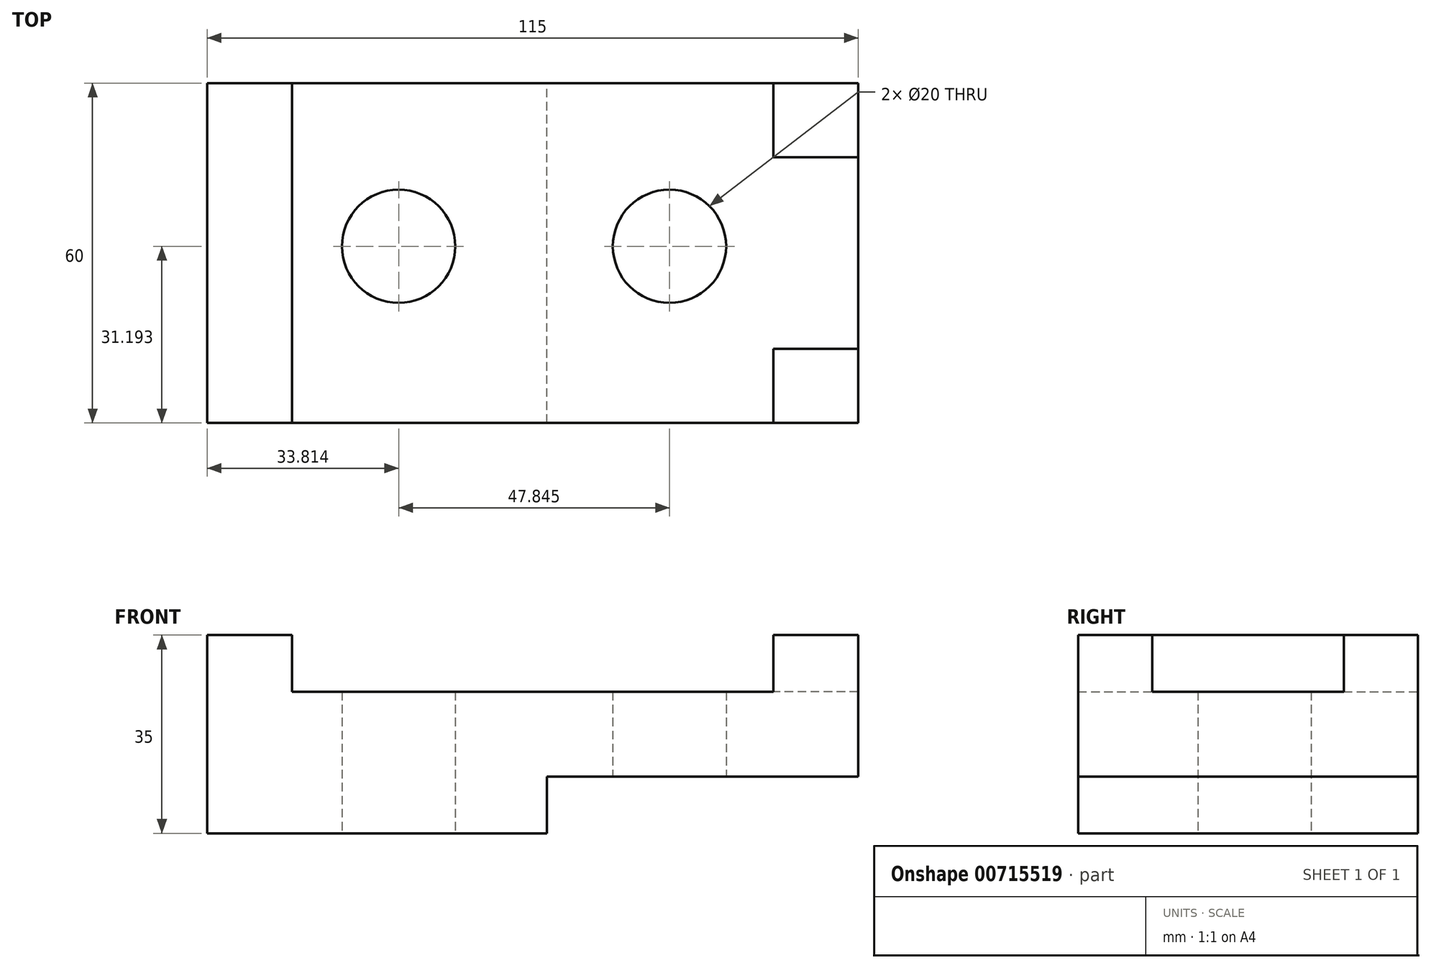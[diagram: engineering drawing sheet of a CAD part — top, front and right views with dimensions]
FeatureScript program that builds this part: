
annotation { "Feature Type Name" : "Feature", "Feature Type Description" : "" }
export const myFeature = defineFeature(function(context is Context, id is Id, definition is map)
    precondition{}
    {
        {
            var Q0;
            Q0=qCreatedBy(makeId("Front.planeOp"),FACE);
            var sketch = newSketch(context, id + "F0", { "sketchPlane" : qUnion([Q0])});
            skLineSegment(sketch, "E0", {"start": v(-60, 0) * mm, "end": v(0, 0) * mm});
            skLineSegment(sketch, "E1", {"start": v(0, 0) * mm, "end": v(0, 10) * mm});
            skLineSegment(sketch, "E2", {"start": v(0, 10) * mm, "end": v(55, 10) * mm});
            skLineSegment(sketch, "E3", {"start": v(-60, 0) * mm, "end": v(-60, 35) * mm});
            skLineSegment(sketch, "E4", {"start": v(-60, 35) * mm, "end": v(-45, 35) * mm});
            skLineSegment(sketch, "E5", {"start": v(-45, 35) * mm, "end": v(-45, 25) * mm});
            skLineSegment(sketch, "E6", {"start": v(-45, 25) * mm, "end": v(40, 25) * mm});
            skLineSegment(sketch, "E7", {"start": v(40, 25) * mm, "end": v(40, 35) * mm});
            skLineSegment(sketch, "E8", {"start": v(40, 35) * mm, "end": v(55, 35) * mm});
            skLineSegment(sketch, "E9", {"start": v(55, 35) * mm, "end": v(55, 10) * mm});
            skSolve(sketch);
        }
        {
            var Q0;
            Q0=makeQuery(id+"F0.imprint","IMPRINT",FACE,{"disambiguationData":[TD([[makeQuery(id+"F0.imprint","IMPRINT",EDGE,{"derivedFrom":sQuery(id+"F0.wireOp",EDGE,"E0")}),1.0]])]});
            extrude(context, id + "F1", {"entities" : qUnion([Q0]), "depth" : 60 * mm, "offsetDistance" : 25 * mm});
        }
        {
            var Q0;
            Q0=qCreatedBy(makeId("Top.planeOp"),FACE);
            var sketch = newSketch(context, id + "F2", { "sketchPlane" : qUnion([Q0])});
            skCircle(sketch, "E10", {"center": v(-26.19, -28.8) * mm, "radius": 10 * mm});
            skCircle(sketch, "E11", {"center": v(21.66, -28.8) * mm, "radius": 10 * mm});
            skSolve(sketch);
        }
        {
            var Q0;
            Q0 = qSketchRegion(id + "F2", true);
            extrude(context, id + "F3", {"entities" : qUnion([Q0]), "operationType" : NewBodyOperationType.REMOVE, "depth" : 34.8 * mm, "offsetDistance" : 25 * mm});
        }
        {
            var Q0;
            Q0=makeQuery(id+"F1.opExtrude","SWEPT_FACE",FACE,{"disambiguationData":[OSD([sQuery(id+"F0.wireOp",EDGE,"E8")])]});
            var sketch = newSketch(context, id + "F4", { "sketchPlane" : qUnion([Q0])});
            skLineSegment(sketch, "E12.bottom", {"start": v(55, -13.07) * mm, "end": v(25, -13.07) * mm});
            skLineSegment(sketch, "E12.top", {"start": v(55, -46.93) * mm, "end": v(25, -46.93) * mm});
            skLineSegment(sketch, "E12.left", {"start": v(55, -13.07) * mm, "end": v(55, -46.93) * mm});
            skLineSegment(sketch, "E12.right", {"start": v(25, -13.07) * mm, "end": v(25, -46.93) * mm});
            skPoint(sketch, "E12.middle", {"position": v(40, -30) * mm});
            skSolve(sketch);
        }
        {
            var Q0;
            {var subQ0=sQuery(id+"F4.wireOp",EDGE,"E12.left");Q0=makeQuery(id+"F4.imprint","IMPRINT",FACE,{"disambiguationData":[TD([[makeQuery(id+"F4.imprint","IMPRINT",EDGE,{"derivedFrom":subQ0}),1.0]])]});}
            extrude(context, id + "F5", {"entities" : qUnion([Q0]), "operationType" : NewBodyOperationType.REMOVE, "oppositeDirection" : true, "depth" : 10 * mm, "offsetDistance" : 25 * mm});
        }
    });
